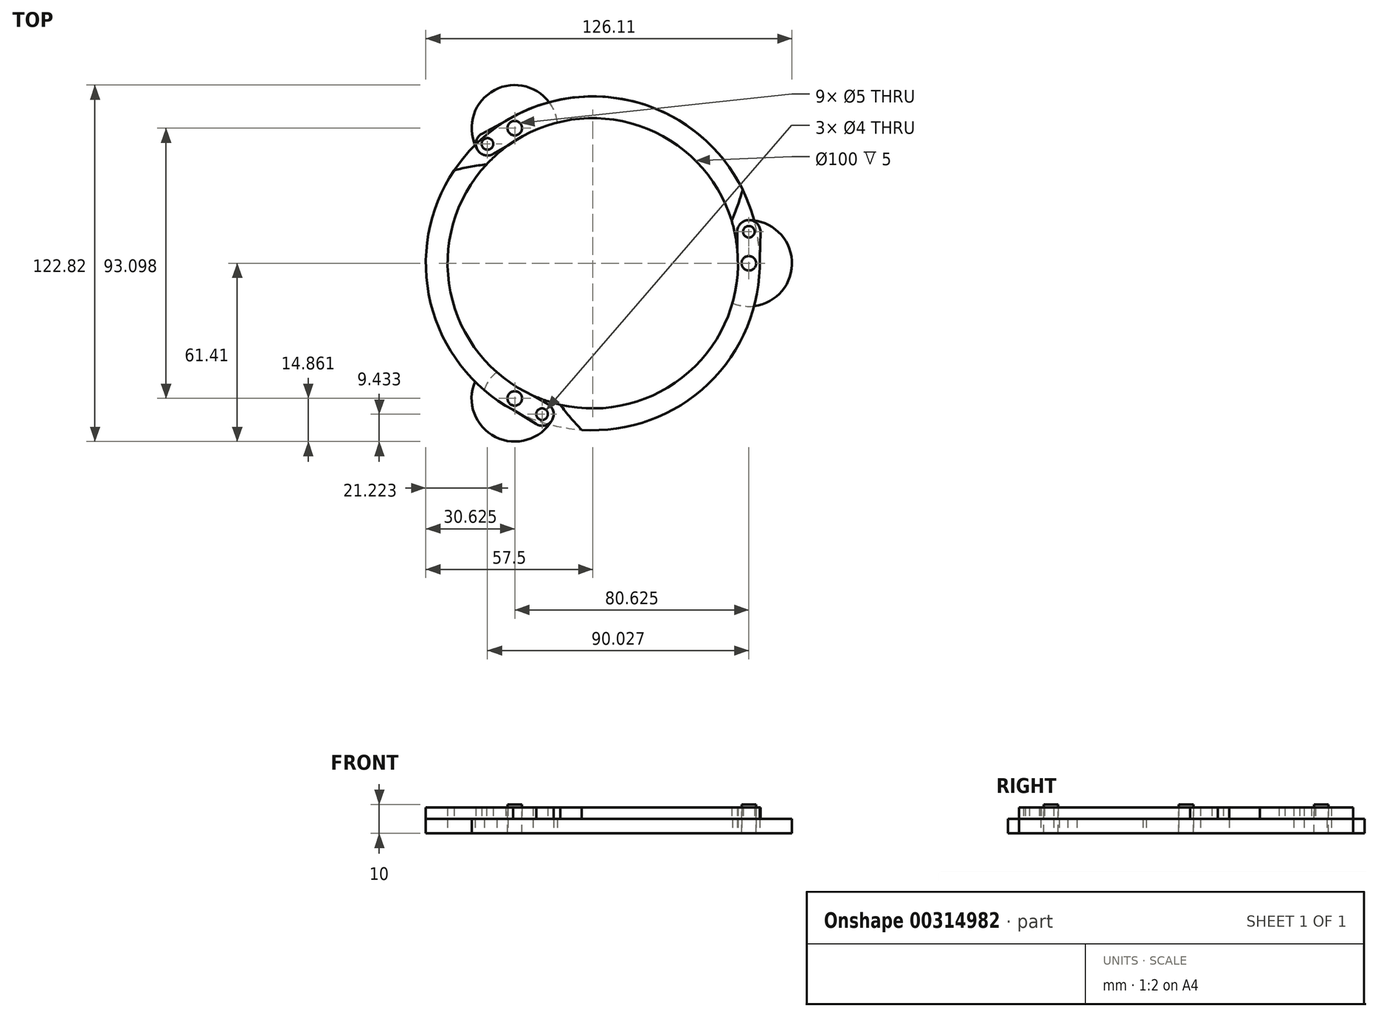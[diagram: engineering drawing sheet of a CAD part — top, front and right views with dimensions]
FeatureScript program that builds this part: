
annotation { "Feature Type Name" : "Feature", "Feature Type Description" : "" }
export const myFeature = defineFeature(function(context is Context, id is Id, definition is map)
    precondition{}
    {
        {
            var Q0;
            Q0=qCreatedBy(makeId("Top.planeOp"),FACE);
            var sketch = newSketch(context, id + "F0", { "sketchPlane" : qUnion([Q0])});
            skCircle(sketch, "E0", {"center": v(0, 0) * mm, "radius": 50 * mm});
            skCircle(sketch, "E1", {"center": v(0, 0) * mm, "radius": 57.5 * mm});
            skSolve(sketch);
        }
        {
            var Q0;
            Q0=makeQuery(id+"F0.imprint","IMPRINT",FACE,{"disambiguationData":[TD([[makeQuery(id+"F0.imprint","IMPRINT",EDGE,{"derivedFrom":sQuery(id+"F0.wireOp",EDGE,"E0")}),-1.0]])]});
            extrude(context, id + "F1", {"entities" : qUnion([Q0]), "depth" : 5 * mm});
        }
        {
            var Q0;
            Q0=makeQuery(id+"F1.opExtrude","CAP_FACE",FACE,{"disambiguationData":[OSD([sQuery(id+"F0.wireOp",EDGE,"E0"),sQuery(id+"F0.wireOp",EDGE,"E1")])],"isStart":false});
            var sketch = newSketch(context, id + "F2", { "sketchPlane" : qUnion([Q0])});
            skLineSegment(sketch, "E2.0", {"start": v(-26.87, 46.55) * mm, "end": v(53.75, 0) * mm, "construction": true});
            skLineSegment(sketch, "E2.1", {"start": v(53.75, 0) * mm, "end": v(-26.87, -46.55) * mm, "construction": true});
            skLineSegment(sketch, "E2.2", {"start": v(-26.88, -46.55) * mm, "end": v(-26.87, 46.55) * mm, "construction": true});
            skCircle(sketch, "E3", {"center": v(-26.87, 46.55) * mm, "radius": 2.5 * mm});
            skCircle(sketch, "E4", {"center": v(-26.88, -46.55) * mm, "radius": 2.5 * mm});
            skCircle(sketch, "E5", {"center": v(53.75, 0) * mm, "radius": 2.5 * mm});
            skCircle(sketch, "E6", {"center": v(-26.87, 46.55) * mm, "radius": 4 * mm});
            skCircle(sketch, "E7", {"center": v(53.75, 0) * mm, "radius": 4 * mm});
            skCircle(sketch, "E8", {"center": v(-26.88, -46.55) * mm, "radius": 4 * mm});
            skArc(sketch, "E9.trimOffspring", {"start": v(-15.66, 40.07) * mm, "mid": v(-26.88, -0.13) * mm, "end": v(-16.5, -40.55) * mm});
            skArc(sketch, "E10.trimOffspring", {"start": v(42.54, -6.47) * mm, "mid": v(13.33, 23.34) * mm, "end": v(-26.88, 34.56) * mm});
            skArc(sketch, "E11.trimOffspring", {"start": v(-20.08, -33.38) * mm, "mid": v(16.48, -21.48) * mm, "end": v(43.37, 6) * mm});
            skArc(sketch, "E12", {"start": v(47.65, 14.3) * mm, "mid": v(-49.22, -7.23) * mm, "end": v(49.75, 0) * mm});
            skArc(sketch, "E13.trimOffspring", {"start": v(47.65, 14.3) * mm, "mid": v(49.9, 19.93) * mm, "end": v(51.72, 25.7) * mm});
            skArc(sketch, "E14.trimOffspring", {"start": v(-36.21, 34.11) * mm, "mid": v(-42.2, 33.25) * mm, "end": v(-48.12, 31.94) * mm});
            skArc(sketch, "E15.trimOffspring", {"start": v(-11.44, -48.42) * mm, "mid": v(-7.7, -53.17) * mm, "end": v(-3.6, -57.64) * mm});
            skLineSegment(sketch, "E16", {"start": v(57.75, 0) * mm, "end": v(57.75, 10.86) * mm});
            skPoint(sketch, "E17", {"position": v(53.75, 10.86) * mm});
            skCircle(sketch, "E18", {"center": v(53.75, 10.86) * mm, "radius": 2 * mm});
            skCircle(sketch, "E19", {"center": v(53.75, 10.86) * mm, "radius": 4 * mm});
            skPoint(sketch, "E20.orphan", {"position": v(49.75, 14.5) * mm});
            skPoint(sketch, "E21.orphan", {"position": v(57.75, 14.5) * mm});
            skArc(sketch, "E22.trimOffspring", {"start": v(49.9, 19.96) * mm, "mid": v(-52.78, -10.16) * mm, "end": v(53.75, 0) * mm, "construction": true});
            skArc(sketch, "E23.trimOffspring", {"start": v(51.72, 25.7) * mm, "mid": v(-56.22, -13.2) * mm, "end": v(57.75, 0) * mm});
            skArc(sketch, "E24.trimOffspring", {"start": v(51.72, 25.7) * mm, "mid": v(-48.12, 31.94) * mm, "end": v(-3.6, -57.64) * mm});
            skLineSegment(sketch, "E25", {"start": v(49.75, 0) * mm, "end": v(49.75, 10.86) * mm});
            skSolve(sketch);
        }
        {
            var Q0;
            {var subQ0=sQuery(id+"F2.wireOp",EDGE,"E16");Q0=makeQuery(id+"F2.imprint","IMPRINT",FACE,{"disambiguationData":[TD([[makeQuery(id+"F2.imprint","IMPRINT",EDGE,{"derivedFrom":subQ0}),1.0]])]});}
            var Q1;
            {var subQ0=sQuery(id+"F2.wireOp",EDGE,"E7");var subQ5=makeQuery(id+"F1.opExtrude","CAP_EDGE",EDGE,{"disambiguationData":[OSD([sQuery(id+"F0.wireOp",EDGE,"E1")])],"isStart":false});var subQ6=makeQuery(id+"F2.imprint","INTERSECT",VERTEX,{"disambiguationData":[OD(0.0)],"derivedFrom":[subQ5,subQ0]});Q1=makeQuery(id+"F2.imprint","IMPRINT",FACE,{"disambiguationData":[TD([[makeQuery(id+"F2.imprint","IMPRINT",EDGE,{"disambiguationData":[TD([[subQ6,-1.0]])],"derivedFrom":subQ0}),-1.0]])]});}
            var Q2;
            Q2=makeQuery(id+"F2.imprint","IMPRINT",FACE,{"disambiguationData":[TD([[makeQuery(id+"F2.imprint","IMPRINT",EDGE,{"derivedFrom":sQuery(id+"F2.wireOp",EDGE,"E18")}),-1.0]])]});
            var Q3;
            {var subQ0=sQuery(id+"F2.wireOp",EDGE,"E19");var subQ1=makeQuery(id+"F2.imprint","INTERSECT",VERTEX,{"derivedFrom":[sQuery(id+"F2.wireOp",EDGE,"E16"),subQ0]});Q3=makeQuery(id+"F2.imprint","IMPRINT",FACE,{"disambiguationData":[TD([[makeQuery(id+"F2.imprint","IMPRINT",EDGE,{"disambiguationData":[TD([[subQ1,-1.0]])],"derivedFrom":subQ0}),1.0]])]});}
            var Q4;
            Q4=makeQuery(id+"F2.imprint","IMPRINT",FACE,{"disambiguationData":[TD([[makeQuery(id+"F2.imprint","IMPRINT",EDGE,{"derivedFrom":sQuery(id+"F2.wireOp",EDGE,"E5")}),-1.0]])]});
            var Q5;
            {var subQ0=sQuery(id+"F2.wireOp",EDGE,"E7");var subQ1=makeQuery(id+"F1.opExtrude","CAP_EDGE",EDGE,{"disambiguationData":[OSD([sQuery(id+"F0.wireOp",EDGE,"E0")])],"isStart":false});var subQ2=makeQuery(id+"F2.imprint","INTERSECT",VERTEX,{"disambiguationData":[OD(1.0)],"derivedFrom":[subQ1,subQ0]});Q5=makeQuery(id+"F2.imprint","IMPRINT",FACE,{"disambiguationData":[TD([[makeQuery(id+"F2.imprint","IMPRINT",EDGE,{"disambiguationData":[TD([[subQ2,-1.0]])],"derivedFrom":subQ0}),-1.0]])]});}
            extrude(context, id + "F3", {"entities" : qUnion([Q0, Q1, Q2, Q3, Q4, Q5]), "depth" : 4 * mm});
        }
        {
            var Q0;
            Q0=makeQuery(id+"F3.opExtrude","CAP_FACE",FACE,{"disambiguationData":[OSD([sQuery(id+"F0.wireOp",EDGE,"E0"),sQuery(id+"F0.wireOp",EDGE,"E1"),sQuery(id+"F2.wireOp",EDGE,"E5"),sQuery(id+"F2.wireOp",EDGE,"E7"),sQuery(id+"F2.wireOp",EDGE,"E15.trimOffspring"),sQuery(id+"F2.wireOp",EDGE,"E16"),sQuery(id+"F2.wireOp",EDGE,"E18"),sQuery(id+"F2.wireOp",EDGE,"E19"),sQuery(id+"F2.wireOp",EDGE,"E25")])],"isStart":false});
            var sketch = newSketch(context, id + "F4", { "sketchPlane" : qUnion([Q0])});
            skArc(sketch, "E26.0", {"start": v(-3.86, -57.37) * mm, "mid": v(39.8, -41.5) * mm, "end": v(57.48, 1.44) * mm});
            skLineSegment(sketch, "E27.0", {"start": v(57.75, 0) * mm, "end": v(57.75, 10.86) * mm});
            skLineSegment(sketch, "E28", {"start": v(57.48, 1.44) * mm, "end": v(57.75, 10.86) * mm});
            skLineSegment(sketch, "E29", {"start": v(57.75, 10.86) * mm, "end": v(61.87, 10.74) * mm});
            skLineSegment(sketch, "E30", {"start": v(61.87, 10.74) * mm, "end": v(59.83, -1.35) * mm});
            skLineSegment(sketch, "E31", {"start": v(59.83, -1.35) * mm, "end": v(57.5, -0.2) * mm});
            skSolve(sketch);
        }
        {
            var Q0;
            Q0=makeQuery(id+"F4.imprint","IMPRINT",FACE,{"disambiguationData":[TD([[makeQuery(id+"F4.imprint","IMPRINT",EDGE,{"derivedFrom":sQuery(id+"F4.wireOp",EDGE,"E27.0")}),1.0]])]});
            var Q1;
            Q1=makeQuery(id+"F4.imprint","IMPRINT",FACE,{"disambiguationData":[TD([[makeQuery(id+"F4.imprint","IMPRINT",EDGE,{"derivedFrom":sQuery(id+"F4.wireOp",EDGE,"E27.0")}),-1.0]])]});
            extrude(context, id + "F5", {"entities" : qUnion([Q0, Q1]), "operationType" : NewBodyOperationType.REMOVE, "oppositeDirection" : true, "depth" : 25 * mm});
        }
        {
            var Q0;
            Q0=makeQuery(id+"F1.opExtrude","CAP_FACE",FACE,{"disambiguationData":[OSD([sQuery(id+"F0.wireOp",EDGE,"E0"),sQuery(id+"F0.wireOp",EDGE,"E1")])],"isStart":false});
            var sketch = newSketch(context, id + "F6", { "sketchPlane" : qUnion([Q0])});
            skCircle(sketch, "E32.0", {"center": v(53.75, 0) * mm, "radius": 2.5 * mm});
            skSolve(sketch);
        }
        {
            var Q0;
            Q0=makeQuery(id+"F6.imprint","IMPRINT",FACE,{"disambiguationData":[TD([[makeQuery(id+"F6.imprint","IMPRINT",EDGE,{"derivedFrom":sQuery(id+"F6.wireOp",EDGE,"E32.0")}),1.0]])]});
            extrude(context, id + "F7", {"entities" : qUnion([Q0]), "operationType" : NewBodyOperationType.REMOVE, "oppositeDirection" : true, "depth" : 25 * mm});
        }
        {
            var Q0;
            Q0=makeQuery(id+"F3.opExtrude","SWEPT_BODY",BODY,{"disambiguationData":[OSD([sQuery(id+"F0.wireOp",EDGE,"E0"),sQuery(id+"F0.wireOp",EDGE,"E1"),sQuery(id+"F2.wireOp",EDGE,"E5"),sQuery(id+"F2.wireOp",EDGE,"E7"),sQuery(id+"F2.wireOp",EDGE,"E15.trimOffspring"),sQuery(id+"F2.wireOp",EDGE,"E16"),sQuery(id+"F2.wireOp",EDGE,"E18"),sQuery(id+"F2.wireOp",EDGE,"E19"),sQuery(id+"F2.wireOp",EDGE,"E25")])]});
            var Q1;
            Q1=makeQuery(id+"F1.opExtrude","CAP_EDGE",EDGE,{"disambiguationData":[OSD([sQuery(id+"F0.wireOp",EDGE,"E0")])],"isStart":true});
            circularPattern(context, id + "F8", {"entities" : qUnion([Q0]), "axis" : qUnion([Q1]), "angle" : 360 * degree, "instanceCount" : 3, "equalSpace" : true});
        }
        {
            var Q0;
            Q0=makeQuery(id+"F8.opPattern","COPY",FACE,{"derivedFrom":makeQuery(id+"F3.opExtrude","CAP_FACE",FACE,{"disambiguationData":[OSD([sQuery(id+"F0.wireOp",EDGE,"E0"),sQuery(id+"F0.wireOp",EDGE,"E1"),sQuery(id+"F2.wireOp",EDGE,"E5"),sQuery(id+"F2.wireOp",EDGE,"E7"),sQuery(id+"F2.wireOp",EDGE,"E15.trimOffspring"),sQuery(id+"F2.wireOp",EDGE,"E16"),sQuery(id+"F2.wireOp",EDGE,"E18"),sQuery(id+"F2.wireOp",EDGE,"E19"),sQuery(id+"F2.wireOp",EDGE,"E25")])],"isStart":false}),"instanceName":"2"});
            var sketch = newSketch(context, id + "F9", { "sketchPlane" : qUnion([Q0])});
            skCircle(sketch, "E33.0", {"center": v(-26.88, -46.55) * mm, "radius": 2.5 * mm});
            skCircle(sketch, "E34.0", {"center": v(-26.87, 46.55) * mm, "radius": 2.5 * mm});
            skSolve(sketch);
        }
        {
            var Q0;
            Q0=makeQuery(id+"F9.imprint","IMPRINT",FACE,{"disambiguationData":[TD([[makeQuery(id+"F9.imprint","IMPRINT",EDGE,{"derivedFrom":sQuery(id+"F9.wireOp",EDGE,"E34.0")}),1.0]])]});
            var Q1;
            Q1=makeQuery(id+"F9.imprint","IMPRINT",FACE,{"disambiguationData":[TD([[makeQuery(id+"F9.imprint","IMPRINT",EDGE,{"derivedFrom":sQuery(id+"F9.wireOp",EDGE,"E33.0")}),1.0]])]});
            extrude(context, id + "F10", {"entities" : qUnion([Q0, Q1]), "operationType" : NewBodyOperationType.REMOVE, "oppositeDirection" : true, "depth" : 25 * mm});
        }
        {
            var Q0;
            Q0=makeQuery(id+"F8.opPattern","COPY",FACE,{"derivedFrom":makeQuery(id+"F3.opExtrude","CAP_FACE",FACE,{"disambiguationData":[OSD([sQuery(id+"F0.wireOp",EDGE,"E0"),sQuery(id+"F0.wireOp",EDGE,"E1"),sQuery(id+"F2.wireOp",EDGE,"E5"),sQuery(id+"F2.wireOp",EDGE,"E7"),sQuery(id+"F2.wireOp",EDGE,"E15.trimOffspring"),sQuery(id+"F2.wireOp",EDGE,"E16"),sQuery(id+"F2.wireOp",EDGE,"E18"),sQuery(id+"F2.wireOp",EDGE,"E19"),sQuery(id+"F2.wireOp",EDGE,"E25")])],"isStart":false}),"instanceName":"1"});
            var sketch = newSketch(context, id + "F11", { "sketchPlane" : qUnion([Q0])});
            skCircle(sketch, "E35.0", {"center": v(-26.87, 46.55) * mm, "radius": 2.5 * mm});
            skCircle(sketch, "E35.1", {"center": v(-26.88, -46.55) * mm, "radius": 2.5 * mm});
            skCircle(sketch, "E35.2", {"center": v(53.75, 0) * mm, "radius": 2.5 * mm});
            skSolve(sketch);
        }
        {
            var Q0;
            Q0=makeQuery(id+"F11.imprint","IMPRINT",FACE,{"disambiguationData":[TD([[makeQuery(id+"F11.imprint","IMPRINT",EDGE,{"derivedFrom":sQuery(id+"F11.wireOp",EDGE,"E35.0")}),1.0]])]});
            var Q1;
            Q1=makeQuery(id+"F11.imprint","IMPRINT",FACE,{"disambiguationData":[TD([[makeQuery(id+"F11.imprint","IMPRINT",EDGE,{"derivedFrom":sQuery(id+"F11.wireOp",EDGE,"E35.2")}),1.0]])]});
            var Q2;
            Q2=makeQuery(id+"F11.imprint","IMPRINT",FACE,{"disambiguationData":[TD([[makeQuery(id+"F11.imprint","IMPRINT",EDGE,{"derivedFrom":sQuery(id+"F11.wireOp",EDGE,"E35.1")}),1.0]])]});
            extrude(context, id + "F12", {"entities" : qUnion([Q0, Q1, Q2]), "oppositeDirection" : true, "depth" : 9 * mm, "hasSecondDirection" : true, "secondDirectionOppositeDirection" : false, "secondDirectionDepth" : 1 * mm});
        }
        {
            var Q0;
            Q0=qCreatedBy(makeId("Top.planeOp"),FACE);
            var sketch = newSketch(context, id + "F13", { "sketchPlane" : qUnion([Q0])});
            skArc(sketch, "E36.0.0", {"start": v(51.62, 25.34) * mm, "mid": v(16.05, 55.21) * mm, "end": v(-29.99, 49.06) * mm});
            skLineSegment(sketch, "E36.0.1", {"start": v(-29.99, 49.06) * mm, "end": v(-38.28, 44.58) * mm});
            skArc(sketch, "E36.0.2", {"start": v(-38.28, 44.58) * mm, "mid": v(-39.74, 39.12) * mm, "end": v(-34.28, 37.66) * mm});
            skLineSegment(sketch, "E36.0.3", {"start": v(-34.28, 37.66) * mm, "end": v(-29.2, 40.59) * mm});
            skArc(sketch, "E36.0.4", {"start": v(-29.2, 40.59) * mm, "mid": v(15.96, 47.39) * mm, "end": v(47.8, 14.66) * mm});
            skArc(sketch, "E36.0.5", {"start": v(47.8, 14.66) * mm, "mid": v(49.9, 19.93) * mm, "end": v(51.62, 25.34) * mm});
            skArc(sketch, "E36.1.0", {"start": v(-47.75, 32.03) * mm, "mid": v(-55.84, -13.7) * mm, "end": v(-27.5, -50.5) * mm});
            skLineSegment(sketch, "E36.1.1", {"start": v(-27.5, -50.5) * mm, "end": v(-19.47, -55.44) * mm});
            skArc(sketch, "E36.1.2", {"start": v(-19.47, -55.44) * mm, "mid": v(-14, -53.98) * mm, "end": v(-15.47, -48.51) * mm});
            skLineSegment(sketch, "E36.1.3", {"start": v(-15.47, -48.51) * mm, "end": v(-20.55, -45.58) * mm});
            skArc(sketch, "E36.1.4", {"start": v(-20.55, -45.58) * mm, "mid": v(-49.02, -9.87) * mm, "end": v(-36.6, 34.07) * mm});
            skArc(sketch, "E36.1.5", {"start": v(-36.6, 34.07) * mm, "mid": v(-42.2, 33.25) * mm, "end": v(-47.75, 32.03) * mm});
            skArc(sketch, "E36.2.0", {"start": v(-3.86, -57.37) * mm, "mid": v(39.8, -41.5) * mm, "end": v(57.48, 1.44) * mm});
            skLineSegment(sketch, "E36.2.1", {"start": v(57.48, 1.44) * mm, "end": v(57.75, 10.86) * mm});
            skArc(sketch, "E36.2.2", {"start": v(57.75, 10.86) * mm, "mid": v(53.75, 14.86) * mm, "end": v(49.75, 10.86) * mm});
            skLineSegment(sketch, "E36.2.3", {"start": v(49.75, 10.86) * mm, "end": v(49.75, 5) * mm});
            skArc(sketch, "E36.2.4", {"start": v(49.75, 5) * mm, "mid": v(33.06, -37.51) * mm, "end": v(-11.21, -48.73) * mm});
            skArc(sketch, "E36.2.5", {"start": v(-11.21, -48.73) * mm, "mid": v(-7.69, -53.18) * mm, "end": v(-3.86, -57.37) * mm});
            skCircle(sketch, "E37.0", {"center": v(-26.87, 46.55) * mm, "radius": 2.5 * mm});
            skCircle(sketch, "E38.0.0", {"center": v(-26.88, -46.55) * mm, "radius": 2.5 * mm});
            skCircle(sketch, "E39.0", {"center": v(53.75, 0) * mm, "radius": 2.5 * mm});
            skArc(sketch, "E40", {"start": v(49.03, -9.78) * mm, "mid": v(64.6, -0.4) * mm, "end": v(49.75, 10.1) * mm});
            skArc(sketch, "E41", {"start": v(48.08, -13.73) * mm, "mid": v(68.32, -2.9) * mm, "end": v(53.75, 14.86) * mm});
            skArc(sketch, "E42", {"start": v(-12.15, 48.5) * mm, "mid": v(-31.66, 60.61) * mm, "end": v(-39.74, 39.12) * mm});
            skArc(sketch, "E43", {"start": v(-16.05, 47.35) * mm, "mid": v(-31.96, 56.14) * mm, "end": v(-33.62, 38.04) * mm});
            skArc(sketch, "E44", {"start": v(-40.56, -40.76) * mm, "mid": v(-33.5, -59.85) * mm, "end": v(-14, -53.98) * mm});
            skArc(sketch, "E45", {"start": v(-32.99, -37.58) * mm, "mid": v(-32.64, -55.75) * mm, "end": v(-16.13, -48.13) * mm});
            skSolve(sketch);
        }
        {
            var Q0;
            {var subQ0=sQuery(id+"F13.wireOp",EDGE,"E42");var subQ3=sQuery(id+"F13.wireOp",EDGE,"E36.0.0");var subQ4=makeQuery(id+"F13.imprint","INTERSECT",VERTEX,{"derivedFrom":[subQ3,subQ0]});Q0=makeQuery(id+"F13.imprint","IMPRINT",FACE,{"disambiguationData":[TD([[makeQuery(id+"F13.imprint","IMPRINT",EDGE,{"disambiguationData":[TD([[subQ4,-1.0]])],"derivedFrom":subQ3}),-1.0]])]});}
            var Q1;
            {var subQ0=sQuery(id+"F13.wireOp",EDGE,"E36.0.1");var subQ1=sQuery(id+"F13.wireOp",EDGE,"E36.0.0");var subQ2=makeQuery(id+"F13.imprint","INTERSECT",VERTEX,{"derivedFrom":[subQ1,subQ0]});Q1=makeQuery(id+"F13.imprint","IMPRINT",FACE,{"disambiguationData":[TD([[makeQuery(id+"F13.imprint","IMPRINT",EDGE,{"disambiguationData":[TD([[subQ2,1.0]])],"derivedFrom":subQ1}),-1.0]])]});}
            var Q2;
            {var subQ1=sQuery(id+"F13.wireOp",EDGE,"E36.0.2");var subQ6=sQuery(id+"F13.wireOp",EDGE,"E36.0.1");var subQ8=makeQuery(id+"F13.imprint","INTERSECT",VERTEX,{"derivedFrom":[subQ6,subQ1]});Q2=makeQuery(id+"F13.imprint","IMPRINT",FACE,{"disambiguationData":[TD([[makeQuery(id+"F13.imprint","IMPRINT",EDGE,{"disambiguationData":[TD([[subQ8,1.0]])],"derivedFrom":subQ6}),1.0]])]});}
            var Q3;
            Q3=makeQuery(id+"F13.imprint","IMPRINT",FACE,{"disambiguationData":[TD([[makeQuery(id+"F13.imprint","IMPRINT",EDGE,{"derivedFrom":sQuery(id+"F13.wireOp",EDGE,"E37.0")}),-1.0]])]});
            var Q4;
            {var subQ0=sQuery(id+"F13.wireOp",EDGE,"E36.1.1");var subQ1=sQuery(id+"F13.wireOp",EDGE,"E36.1.0");var subQ2=makeQuery(id+"F13.imprint","INTERSECT",VERTEX,{"derivedFrom":[subQ1,subQ0]});Q4=makeQuery(id+"F13.imprint","IMPRINT",FACE,{"disambiguationData":[TD([[makeQuery(id+"F13.imprint","IMPRINT",EDGE,{"disambiguationData":[TD([[subQ2,1.0]])],"derivedFrom":subQ1}),-1.0]])]});}
            var Q5;
            {var subQ0=sQuery(id+"F13.wireOp",EDGE,"E44");Q5=makeQuery(id+"F13.imprint","IMPRINT",FACE,{"disambiguationData":[TD([[makeQuery(id+"F13.imprint","IMPRINT",EDGE,{"derivedFrom":subQ0}),1.0]])]});}
            var Q6;
            {var subQ1=sQuery(id+"F13.wireOp",EDGE,"E36.1.2");var subQ6=sQuery(id+"F13.wireOp",EDGE,"E36.1.1");var subQ7=makeQuery(id+"F13.imprint","INTERSECT",VERTEX,{"derivedFrom":[subQ6,subQ1]});Q6=makeQuery(id+"F13.imprint","IMPRINT",FACE,{"disambiguationData":[TD([[makeQuery(id+"F13.imprint","IMPRINT",EDGE,{"disambiguationData":[TD([[subQ7,1.0]])],"derivedFrom":subQ6}),1.0]])]});}
            var Q7;
            Q7=makeQuery(id+"F13.imprint","IMPRINT",FACE,{"disambiguationData":[TD([[makeQuery(id+"F13.imprint","IMPRINT",EDGE,{"derivedFrom":sQuery(id+"F13.wireOp",EDGE,"E38.0.0")}),-1.0]])]});
            var Q8;
            {var subQ0=sQuery(id+"F13.wireOp",EDGE,"E36.2.1");var subQ1=sQuery(id+"F13.wireOp",EDGE,"E36.2.0");var subQ2=makeQuery(id+"F13.imprint","INTERSECT",VERTEX,{"derivedFrom":[subQ1,subQ0]});Q8=makeQuery(id+"F13.imprint","IMPRINT",FACE,{"disambiguationData":[TD([[makeQuery(id+"F13.imprint","IMPRINT",EDGE,{"disambiguationData":[TD([[subQ2,1.0]])],"derivedFrom":subQ1}),-1.0]])]});}
            var Q9;
            {var subQ1=sQuery(id+"F13.wireOp",EDGE,"E36.2.0");var subQ7=sQuery(id+"F13.wireOp",EDGE,"E41");var subQ9=makeQuery(id+"F13.imprint","INTERSECT",VERTEX,{"derivedFrom":[subQ1,subQ7]});Q9=makeQuery(id+"F13.imprint","IMPRINT",FACE,{"disambiguationData":[TD([[makeQuery(id+"F13.imprint","IMPRINT",EDGE,{"disambiguationData":[TD([[subQ9,-1.0]])],"derivedFrom":subQ1}),-1.0]])]});}
            var Q10;
            {var subQ1=sQuery(id+"F13.wireOp",EDGE,"E36.2.2");var subQ5=sQuery(id+"F13.wireOp",EDGE,"E36.2.1");var subQ8=makeQuery(id+"F13.imprint","INTERSECT",VERTEX,{"derivedFrom":[subQ5,subQ1]});Q10=makeQuery(id+"F13.imprint","IMPRINT",FACE,{"disambiguationData":[TD([[makeQuery(id+"F13.imprint","IMPRINT",EDGE,{"disambiguationData":[TD([[subQ8,1.0]])],"derivedFrom":subQ5}),1.0]])]});}
            var Q11;
            Q11=makeQuery(id+"F13.imprint","IMPRINT",FACE,{"disambiguationData":[TD([[makeQuery(id+"F13.imprint","IMPRINT",EDGE,{"derivedFrom":sQuery(id+"F13.wireOp",EDGE,"E39.0")}),-1.0]])]});
            var Q12;
            {var subQ0=sQuery(id+"F13.wireOp",EDGE,"E41");var subQ1=sQuery(id+"F13.wireOp",EDGE,"E36.2.0");var subQ2=makeQuery(id+"F13.imprint","INTERSECT",VERTEX,{"derivedFrom":[subQ1,subQ0]});Q12=makeQuery(id+"F13.imprint","IMPRINT",FACE,{"disambiguationData":[TD([[makeQuery(id+"F13.imprint","IMPRINT",EDGE,{"disambiguationData":[TD([[subQ2,-1.0]])],"derivedFrom":subQ1}),1.0]])]});}
            var Q13;
            {var subQ0=sQuery(id+"F13.wireOp",EDGE,"E42");var subQ1=sQuery(id+"F13.wireOp",EDGE,"E36.0.0");var subQ2=makeQuery(id+"F13.imprint","INTERSECT",VERTEX,{"derivedFrom":[subQ1,subQ0]});Q13=makeQuery(id+"F13.imprint","IMPRINT",FACE,{"disambiguationData":[TD([[makeQuery(id+"F13.imprint","IMPRINT",EDGE,{"disambiguationData":[TD([[subQ2,-1.0]])],"derivedFrom":subQ1}),1.0]])]});}
            extrude(context, id + "F14", {"entities" : qUnion([Q0, Q1, Q2, Q3, Q4, Q5, Q6, Q7, Q8, Q9, Q10, Q11, Q12, Q13]), "depth" : 5 * mm});
        }
    });
